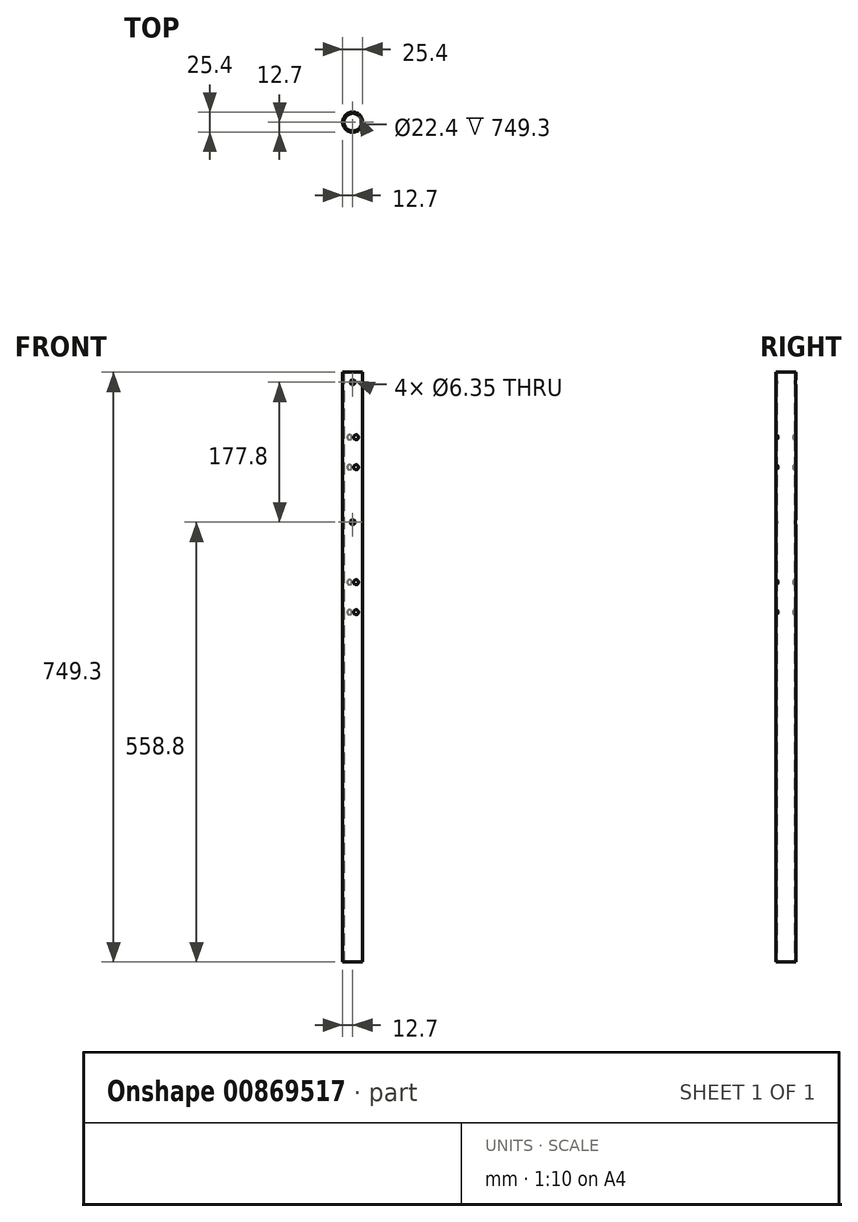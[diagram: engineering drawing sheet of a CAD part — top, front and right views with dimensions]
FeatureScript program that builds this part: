
annotation { "Feature Type Name" : "Feature", "Feature Type Description" : "" }
export const myFeature = defineFeature(function(context is Context, id is Id, definition is map)
    precondition{}
    {
        {
            var Q0;
            Q0=qCreatedBy(makeId("Top.planeOp"),FACE);
            var sketch = newSketch(context, id + "F0", { "sketchPlane" : qUnion([Q0])});
            skCircle(sketch, "E0", {"center": v(0, 0) * mm, "radius": 12.7 * mm});
            skCircle(sketch, "E1.0", {"center": v(0, 0) * mm, "radius": 11.2 * mm});
            skSolve(sketch);
        }
        {
            var Q0;
            Q0=makeQuery(id+"F0.imprint","IMPRINT",FACE,{"disambiguationData":[TD([[makeQuery(id+"F0.imprint","IMPRINT",EDGE,{"derivedFrom":sQuery(id+"F0.wireOp",EDGE,"E0")}),1.0]])]});
            extrude(context, id + "F1", {"entities" : qUnion([Q0]), "depth" : 749.3 * mm, "offsetDistance" : 25.4 * mm});
        }
        {
            var Q0;
            Q0=qCreatedBy(makeId("Front.planeOp"),FACE);
            var sketch = newSketch(context, id + "F2", { "sketchPlane" : qUnion([Q0])});
            skLineSegment(sketch, "E2", {"start": v(0, 0) * mm, "end": v(0, 749.3) * mm, "construction": true});
            skCircle(sketch, "E3", {"center": v(0, 558.8) * mm, "radius": 3.18 * mm});
            skCircle(sketch, "E4", {"center": v(0, 736.6) * mm, "radius": 3.18 * mm});
            skSolve(sketch);
        }
        {
            var Q0;
            Q0 = qSketchRegion(id + "F2", true);
            extrude(context, id + "F3", {"entities" : qUnion([Q0]), "operationType" : NewBodyOperationType.REMOVE, "endBound" : BoundingType.SYMMETRIC, "depth" : 25.4 * mm, "offsetDistance" : 25.4 * mm});
        }
        {
            var Q0;
            Q0=qCreatedBy(makeId("Front.planeOp"),FACE);
            var sketch = newSketch(context, id + "F4", { "sketchPlane" : qUnion([Q0])});
            skLineSegment(sketch, "E5", {"start": v(0, 0) * mm, "end": v(0, 781.06) * mm});
            skSolve(sketch);
        }
        {
            var Q0;
            Q0=sQuery(id+"F4.wireOp",EDGE,"E5");
            cPlane(context, id + "F5", {"entities" : qUnion([Q0]), "cplaneType" : CPlaneType.LINE_ANGLE, "offset" : 25.4 * mm, "angle" : 70 * degree, "oppositeDirection" : true, "width" : 152.4 * mm, "height" : 152.4 * mm});
        }
        {
            var Q0;
            Q0=qCreatedBy(id+"F5.planeOp",FACE);
            var sketch = newSketch(context, id + "F6", { "sketchPlane" : qUnion([Q0])});
            skCircle(sketch, "E6", {"center": v(0, 628.65) * mm, "radius": 3.18 * mm});
            skCircle(sketch, "E7", {"center": v(0, 666.75) * mm, "radius": 3.18 * mm});
            skCircle(sketch, "E8", {"center": v(0, 444.5) * mm, "radius": 3.18 * mm});
            skCircle(sketch, "E9", {"center": v(0, 482.6) * mm, "radius": 3.18 * mm});
            skSolve(sketch);
        }
        {
            var Q0;
            Q0 = qSketchRegion(id + "F6", true);
            extrude(context, id + "F7", {"entities" : qUnion([Q0]), "operationType" : NewBodyOperationType.REMOVE, "endBound" : BoundingType.SYMMETRIC, "oppositeDirection" : true, "depth" : 25.4 * mm, "offsetDistance" : 25.4 * mm});
        }
    });
